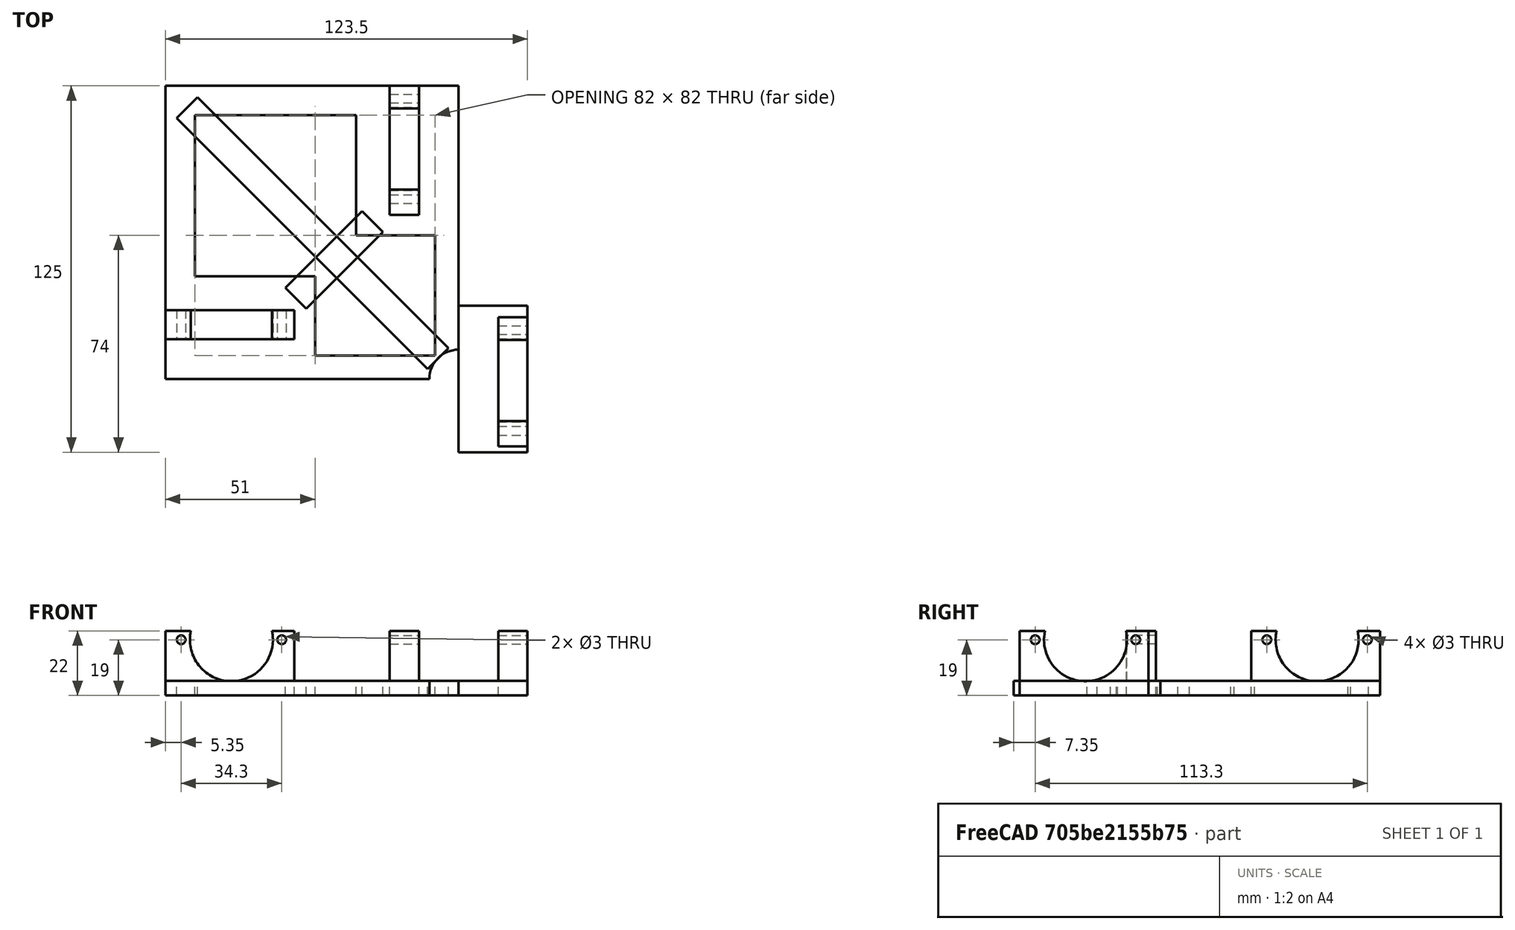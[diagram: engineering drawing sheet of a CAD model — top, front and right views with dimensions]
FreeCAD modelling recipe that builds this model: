
FCSTD DOCUMENT
Label: structure
objects: Part::Cut×8, Part::Box×7, Part::Cylinder×4
note: 19 computed .brp shape members not serialized (recipe doc carries the construction recipe); baked Part::Feature solids carry a one-line shape summary decoded from their .brp

FEATURE [Part::Box] Box
  Height = 5
  Length = 100
  Width = 100
FEATURE [Part::Box] Box001
  Height = 22
  Length = 44
  Placement = pos=(0,13.5,0) rot=(0,0,1;0rad)
  Width = 10
FEATURE [Part::Cylinder] Cylinder001
  Angle = 360
  Height = 10
  Placement = pos=(5.35,23.5,19) rot=(1,0,0;1.5708rad)
  Radius = 1.5
FEATURE [Part::Cylinder] Cylinder001001
  Angle = 360
  Height = 10
  Placement = pos=(39.65,23.5,19) rot=(1,0,0;1.5708rad)
  Radius = 1.5
FEATURE [Part::Cylinder] Cylinder
  Angle = 360
  Height = 10
  Placement = pos=(22.5,23.5,19) rot=(1,0,0;1.5708rad)
  Radius = 14.15
FEATURE [Part::Cut] Cut
  Base = -> Box001
  Tool = -> Cylinder
FEATURE [Part::Cut] Cut001
  Base = -> Cut
  Tool = -> Cylinder001001
FEATURE [Part::Cut] Cut002
  Base = -> Cut001
  Tool = -> Cylinder001
FEATURE [Part::Cut] Cut002001
  Base = -> Cut001
  Placement = pos=(100,56,0) rot=(0,0,1;1.5708rad)
  Tool = -> Cylinder001
FEATURE [Part::Box] Box002
  Height = 5
  Length = 23.5
  Placement = pos=(100,-25,0) rot=(0,0,1;0rad)
  Width = 50
FEATURE [Part::Cut] Cut002001001
  Base = -> Cut001
  Placement = pos=(137,-23,0) rot=(0,0,1;1.5708rad)
  Tool = -> Cylinder001
FEATURE [Part::Cylinder] Cylinder001002
  Angle = 360
  Height = 10
  Placement = pos=(100,0,0) rot=(0,0,1;0rad)
  Radius = 10
FEATURE [Part::Cut] Cut002001002
  Base = -> Box
  Tool = -> Cylinder001002
FEATURE [Part::Box] Box003
  Height = 10
  Length = 55
  Placement = pos=(10,35,0) rot=(0,0,1;0rad)
  Width = 55
FEATURE [Part::Cut] Cut002001003
  Base = -> Cut002001002
  Tool = -> Box003
FEATURE [Part::Box] Box004
  Height = 10
  Length = 41
  Placement = pos=(51,8,0) rot=(0,0,1;0rad)
  Width = 41
FEATURE [Part::Cut] Cut002001004
  Base = -> Cut002001003
  Tool = -> Box004
FEATURE [Part::Box] Box005
  Height = 5
  Length = 121
  Placement = pos=(96.5,10.5,0) rot=(0,0,1;2.3562rad)
  Width = 10
FEATURE [Part::Box] Box006
  Height = 5
  Length = 37
  Placement = pos=(48,24,0) rot=(0,0,1;0.785397rad)
  Width = 10
